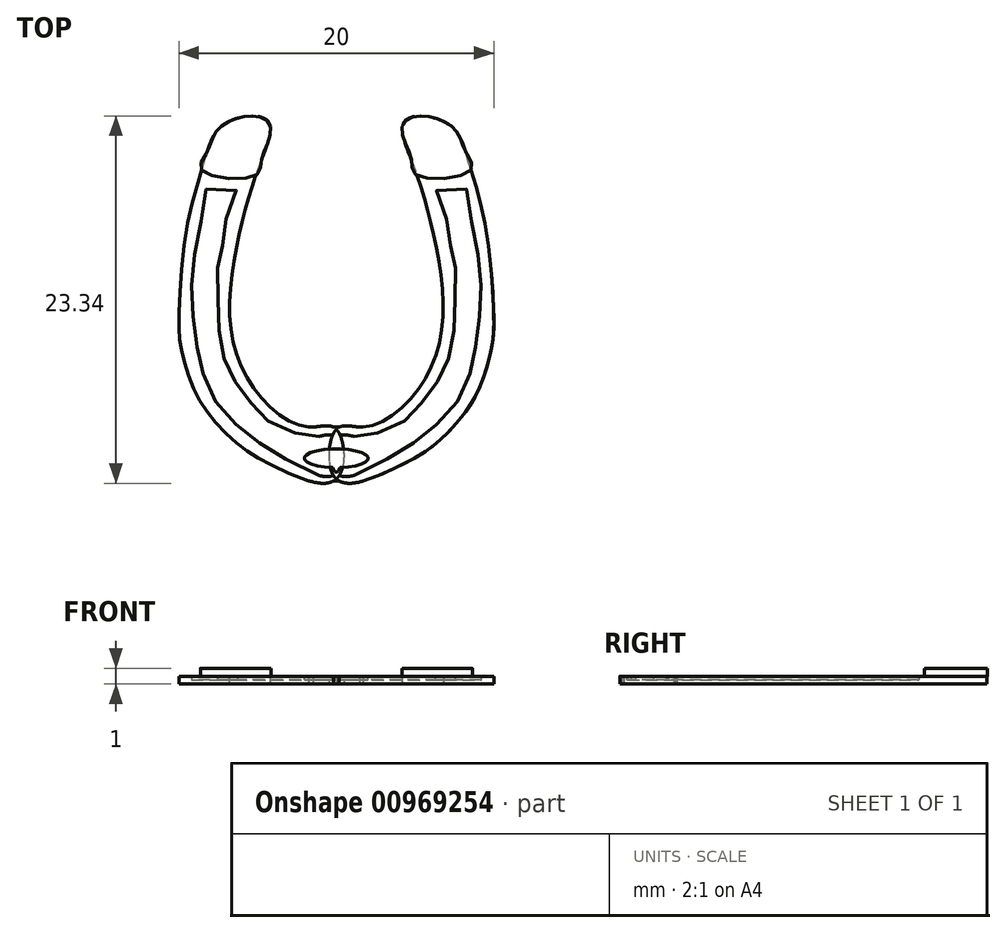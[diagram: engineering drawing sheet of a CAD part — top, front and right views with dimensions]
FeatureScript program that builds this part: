
annotation { "Feature Type Name" : "Feature", "Feature Type Description" : "" }
export const myFeature = defineFeature(function(context is Context, id is Id, definition is map)
    precondition{}
    {
        {
            var Q0;
            Q0=qCreatedBy(makeId("Top.planeOp"),FACE);
            var sketch = newSketch(context, id + "F0", { "sketchPlane" : qUnion([Q0])});
            skLineSegment(sketch, "E0.bottom", {"start": v(-1.78, -6.7) * mm, "end": v(1.7, -6.7) * mm});
            skLineSegment(sketch, "E0.top", {"start": v(-1.7, -10.13) * mm, "end": v(1.7, -10.13) * mm});
            skLineSegment(sketch, "E0.left", {"start": v(-1.78, -6.7) * mm, "end": v(-1.78, -10.1) * mm});
            skLineSegment(sketch, "E0.right", {"start": v(1.7, -6.7) * mm, "end": v(1.7, -10.13) * mm});
            skFitSpline(sketch, "E1.trimOffspring", {"points": [v(-10, 0) * mm, v(-9.47, 6.1) * mm, v(-8.38, 10.18) * mm, v(-7.1, 12.56) * mm, v(-4.37, 12.77) * mm, v(-4.84, 10.04) * mm, v(-6.14, 5.69) * mm, v(-6.75, 0) * mm, v(-4.98, -4.59) * mm, v(-1.78, -6.7) * mm, v(0, -6.83) * mm, v(0, -10) * mm, v(-3.9, -9.2) * mm, v(-6.12, -7.9) * mm, v(-8.02, -5.97) * mm, v(-9.17, -4) * mm, v(-9.85, -1.75) * mm, v(-10, 0) * mm]});
            skFitSpline(sketch, "E2.trimOffspring", {"points": [v(10, 0) * mm, v(9.47, 6.1) * mm, v(8.38, 10.18) * mm, v(7.1, 12.56) * mm, v(4.37, 12.77) * mm, v(4.84, 10.04) * mm, v(6.14, 5.69) * mm, v(6.75, 0) * mm, v(4.98, -4.59) * mm, v(1.78, -6.7) * mm, v(0, -6.83) * mm, v(0, -10) * mm, v(3.9, -9.2) * mm, v(6.12, -7.9) * mm, v(8.02, -5.97) * mm, v(9.17, -4) * mm, v(9.85, -1.75) * mm, v(10, 0) * mm]});
            skSolve(sketch);
        }
        {
            var Q0;
            Q0 = qSketchRegion(id + "F0", true);
            extrude(context, id + "F1", {"entities" : qUnion([Q0]), "endBound" : BoundingType.SYMMETRIC, "depth" : .5 * mm, "offsetDistance" : 25 * mm});
        }
        {
            var Q0;
            Q0=makeQuery(id+"F1.opExtrude","CAP_FACE",FACE,{"disambiguationData":[OSD([sQuery(id+"F0.wireOp",EDGE,"E0.bottom"),sQuery(id+"F0.wireOp",EDGE,"E0.top"),sQuery(id+"F0.wireOp",EDGE,"E0.right"),sQuery(id+"F0.wireOp",EDGE,"E1.trimOffspring"),sQuery(id+"F0.wireOp",EDGE,"E2.trimOffspring")])],"isStart":false});
            var sketch = newSketch(context, id + "F2", { "sketchPlane" : qUnion([Q0])});
            skFitSpline(sketch, "E3", {"points": [v(-8.55, 9.62) * mm, v(-5.13, 9.27) * mm, v(-4.77, 10.23) * mm, v(-4.36, 11.34) * mm, v(-4.22, 12.51) * mm, v(-4.96, 13.03) * mm, v(-6.09, 12.97) * mm, v(-7.12, 12.54) * mm, v(-7.8, 11.8) * mm, v(-8.22, 10.75) * mm, v(-8.55, 9.62) * mm]});
            skFitSpline(sketch, "E4.MirrorC", {"points": [v(8.55, 9.62) * mm, v(5.13, 9.27) * mm, v(4.77, 10.23) * mm, v(4.36, 11.34) * mm, v(4.22, 12.51) * mm, v(4.96, 13.03) * mm, v(6.09, 12.97) * mm, v(7.12, 12.54) * mm, v(7.8, 11.8) * mm, v(8.22, 10.75) * mm, v(8.55, 9.62) * mm]});
            skSolve(sketch);
        }
        {
            var Q0;
            Q0 = qSketchRegion(id + "F2", true);
            extrude(context, id + "F3", {"entities" : qUnion([Q0]), "operationType" : NewBodyOperationType.ADD, "depth" : .5 * mm, "offsetDistance" : 25 * mm});
        }
        {
            var Q0;
            {var subQ0=sQuery(id+"F0.wireOp",EDGE,"E0.right");var subQ1=sQuery(id+"F2.wireOp",EDGE,"E4.MirrorC");var subQ2=sQuery(id+"F0.wireOp",EDGE,"E0.top");var subQ3=sQuery(id+"F0.wireOp",EDGE,"E1.trimOffspring");var subQ4=sQuery(id+"F0.wireOp",EDGE,"E0.bottom");var subQ5=sQuery(id+"F0.wireOp",EDGE,"E2.trimOffspring");var subQ6=sQuery(id+"F2.wireOp",EDGE,"E3");Q0=makeQuery(id+"F3.boolean.opBoolean","SPLIT",FACE,{"disambiguationData":[TD([makeQuery(id+"F1.opExtrude","SWEPT_FACE",FACE,{"disambiguationData":[OSD([subQ4])]}),makeQuery(id+"F1.opExtrude","SWEPT_FACE",FACE,{"disambiguationData":[OSD([subQ2])]}),makeQuery(id+"F1.opExtrude","SWEPT_FACE",FACE,{"disambiguationData":[OSD([subQ0])]}),makeQuery(id+"F1.opExtrude","SWEPT_FACE",FACE,{"disambiguationData":[OSD([subQ3])]}),makeQuery(id+"F1.opExtrude","SWEPT_FACE",FACE,{"disambiguationData":[OSD([subQ5])]}),makeQuery(id+"F3.opExtrude","SWEPT_FACE",FACE,{"disambiguationData":[OSD([subQ6])]}),makeQuery(id+"F3.opExtrude","CAP_FACE",FACE,{"disambiguationData":[OSD([subQ6])],"isStart":true}),makeQuery(id+"F3.opExtrude","SWEPT_FACE",FACE,{"disambiguationData":[OSD([subQ1])]}),makeQuery(id+"F3.opExtrude","CAP_FACE",FACE,{"disambiguationData":[OSD([subQ1])],"isStart":true})])],"derivedFrom":makeQuery(id+"F1.opExtrude","CAP_FACE",FACE,{"disambiguationData":[OSD([subQ4,subQ2,subQ0,subQ3,subQ5])],"isStart":false})});}
            var sketch = newSketch(context, id + "F4", { "sketchPlane" : qUnion([Q0])});
            skEllipse(sketch, "E5", {"center": v(0, -8.95) * mm, "majorRadius": 2.03 * mm, "minorRadius": 0.6 * mm, "majorAxis": v(1, 0)});
            skSolve(sketch);
        }
        {
            var Q0;
            Q0=makeQuery(id+"F4.imprint","IMPRINT",FACE,{"disambiguationData":[TD([[makeQuery(id+"F4.imprint","IMPRINT",EDGE,{"derivedFrom":sQuery(id+"F4.wireOp",EDGE,"E5")}),1.0]])]});
            extrude(context, id + "F5", {"entities" : qUnion([Q0]), "operationType" : NewBodyOperationType.ADD, "oppositeDirection" : true, "depth" : .25 * mm, "offsetDistance" : 25 * mm});
        }
        {
            var Q0;
            {var subQ0=sQuery(id+"F0.wireOp",EDGE,"E0.right");var subQ1=sQuery(id+"F2.wireOp",EDGE,"E4.MirrorC");var subQ2=sQuery(id+"F0.wireOp",EDGE,"E0.top");var subQ3=sQuery(id+"F0.wireOp",EDGE,"E1.trimOffspring");var subQ4=sQuery(id+"F0.wireOp",EDGE,"E0.bottom");var subQ5=sQuery(id+"F0.wireOp",EDGE,"E2.trimOffspring");var subQ6=sQuery(id+"F2.wireOp",EDGE,"E3");Q0=makeQuery(id+"F3.boolean.opBoolean","SPLIT",FACE,{"disambiguationData":[TD([makeQuery(id+"F1.opExtrude","SWEPT_FACE",FACE,{"disambiguationData":[OSD([subQ4])]}),makeQuery(id+"F1.opExtrude","SWEPT_FACE",FACE,{"disambiguationData":[OSD([subQ2])]}),makeQuery(id+"F1.opExtrude","SWEPT_FACE",FACE,{"disambiguationData":[OSD([subQ0])]}),makeQuery(id+"F1.opExtrude","SWEPT_FACE",FACE,{"disambiguationData":[OSD([subQ3])]}),makeQuery(id+"F1.opExtrude","SWEPT_FACE",FACE,{"disambiguationData":[OSD([subQ5])]}),makeQuery(id+"F3.opExtrude","SWEPT_FACE",FACE,{"disambiguationData":[OSD([subQ6])]}),makeQuery(id+"F3.opExtrude","CAP_FACE",FACE,{"disambiguationData":[OSD([subQ6])],"isStart":true}),makeQuery(id+"F3.opExtrude","SWEPT_FACE",FACE,{"disambiguationData":[OSD([subQ1])]}),makeQuery(id+"F3.opExtrude","CAP_FACE",FACE,{"disambiguationData":[OSD([subQ1])],"isStart":true})])],"derivedFrom":makeQuery(id+"F1.opExtrude","CAP_FACE",FACE,{"disambiguationData":[OSD([subQ4,subQ2,subQ0,subQ3,subQ5])],"isStart":false})});}
            var sketch = newSketch(context, id + "F6", { "sketchPlane" : qUnion([Q0])});
            skPoint(sketch, "E6.17.internal.snap0", {"position": v(0, -9.25) * mm});
            skPoint(sketch, "E6.18.internal.snap0", {"position": v(0, -9.25) * mm});
            skLineSegment(sketch, "E7.bottom", {"start": v(-1.11, -7.29) * mm, "end": v(1.11, -7.29) * mm});
            skLineSegment(sketch, "E7.top", {"start": v(-1.11, -9.77) * mm, "end": v(1.11, -9.77) * mm});
            skFitSpline(sketch, "E8.trimOffspring", {"points": [v(8.07, 8.6) * mm, v(6.33, 8.28) * mm, v(6.96, 6.65) * mm, v(7.16, 5.16) * mm, v(7.41, 4.33) * mm, v(7.56, 3.19) * mm, v(7.53, 1.33) * mm, v(7.47, -0.42) * mm, v(7.27, -1.82) * mm, v(6.76, -3.28) * mm, v(6.24, -4.03) * mm, v(5.41, -5.17) * mm, v(4.7, -6.03) * mm, v(3.52, -6.74) * mm, v(1.98, -7.26) * mm, v(1.11, -7.29) * mm, v(0, -7.37) * mm, v(0, -9.64) * mm, v(2.35, -9.25) * mm, v(3.87, -8.3) * mm, v(5.44, -7.35) * mm, v(6.58, -6.32) * mm, v(7.76, -4.95) * mm, v(8.44, -3.4) * mm, v(8.76, -2.06) * mm, v(8.99, -0.6) * mm, v(9.19, 1.4) * mm, v(9.16, 2.92) * mm, v(8.89, 4.9) * mm, v(8.51, 6.94) * mm, v(8.07, 8.6) * mm]});
            skFitSpline(sketch, "E9.trimOffspring", {"points": [v(-8.07, 8.6) * mm, v(-6.33, 8.28) * mm, v(-6.96, 6.65) * mm, v(-7.16, 5.16) * mm, v(-7.41, 4.33) * mm, v(-7.56, 3.19) * mm, v(-7.53, 1.33) * mm, v(-7.47, -0.42) * mm, v(-7.27, -1.82) * mm, v(-6.76, -3.28) * mm, v(-6.24, -4.03) * mm, v(-5.41, -5.17) * mm, v(-4.7, -6.03) * mm, v(-3.52, -6.74) * mm, v(-1.98, -7.26) * mm, v(-1.11, -7.29) * mm, v(0, -7.37) * mm, v(0, -9.64) * mm, v(-2.35, -9.25) * mm, v(-3.87, -8.3) * mm, v(-5.44, -7.35) * mm, v(-6.58, -6.32) * mm, v(-7.76, -4.95) * mm, v(-8.44, -3.4) * mm, v(-8.76, -2.06) * mm, v(-8.99, -0.6) * mm, v(-9.19, 1.4) * mm, v(-9.16, 2.92) * mm, v(-8.89, 4.9) * mm, v(-8.51, 6.94) * mm, v(-8.07, 8.6) * mm]});
            skSolve(sketch);
        }
        {
            var Q0;
            Q0 = qSketchRegion(id + "F6", true);
            extrude(context, id + "F7", {"entities" : qUnion([Q0]), "operationType" : NewBodyOperationType.REMOVE, "oppositeDirection" : true, "depth" : .25 * mm, "offsetDistance" : 25 * mm});
        }
        {
            var Q0;
            Q0=makeQuery(id+"F7.boolean.opBoolean","COPY",FACE,{"derivedFrom":makeQuery(id+"F7.opExtrude","CAP_FACE",FACE,{"disambiguationData":[OSD([sQuery(id+"F6.wireOp",EDGE,"E7.bottom"),sQuery(id+"F6.wireOp",EDGE,"E7.top"),sQuery(id+"F6.wireOp",EDGE,"E8.trimOffspring"),sQuery(id+"F6.wireOp",EDGE,"E9.trimOffspring")])],"isStart":false})});
            var sketch = newSketch(context, id + "F8", { "sketchPlane" : qUnion([Q0])});
            skEllipse(sketch, "E10", {"center": v(0, -8.68) * mm, "majorRadius": 2.03 * mm, "minorRadius": 0.6 * mm, "majorAxis": v(1, 0)});
            skSolve(sketch);
        }
        {
            var Q0;
            Q0 = qSketchRegion(id + "F8", true);
            extrude(context, id + "F9", {"entities" : qUnion([Q0]), "operationType" : NewBodyOperationType.ADD, "depth" : .25 * mm, "offsetDistance" : 25 * mm});
        }
    });
